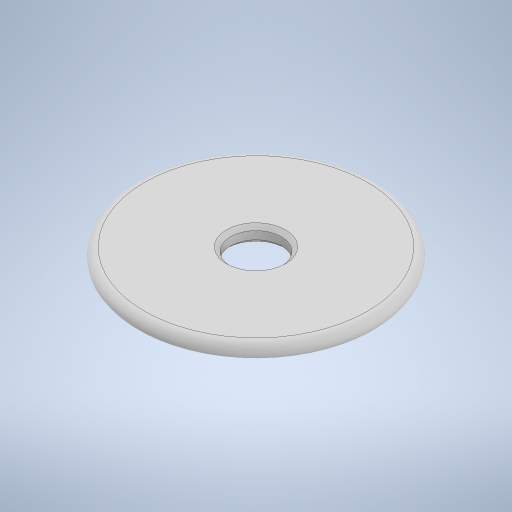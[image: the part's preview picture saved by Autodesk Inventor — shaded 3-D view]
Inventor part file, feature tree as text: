
AUTODESK INVENTOR PART (.ipt)
format: ipt  version: 2023 (Build 270158000, 158)  size: 269,824 bytes
history: native  units: mm
features: extrude x2, sketch x2, plane x1, fillet x1, chamfer x1
ambient origin geometry x8: Origin, YZ Plane, XZ Plane, XY Plane, X Axis, Y Axis, Z Axis, Center Point
bodies: Solid1 (feature_tree)
feature tree (7):
  extrude  "Extrusion1"  Depth=1.0mm TaperAngle=0.0deg
  plane  "Work Plane1"
  extrude  "Extrusion3"  Depth=10.0mm TaperAngle=0.0deg
  fillet  "Fillet2"  Radius=0.5mm
  chamfer  "Chamfer2"  Distance=0.25mm Angle=45.0deg
  sketch  "Sketch1"  dims[d0=15.0mm d1=1.0mm d2=0.0mm]
  sketch  "Sketch3"  dims[d7=3.2mm d8=10.0mm d9=0.0mm d14=0.5mm d15=0.25mm d16=2.0mm d17=45.0deg]
